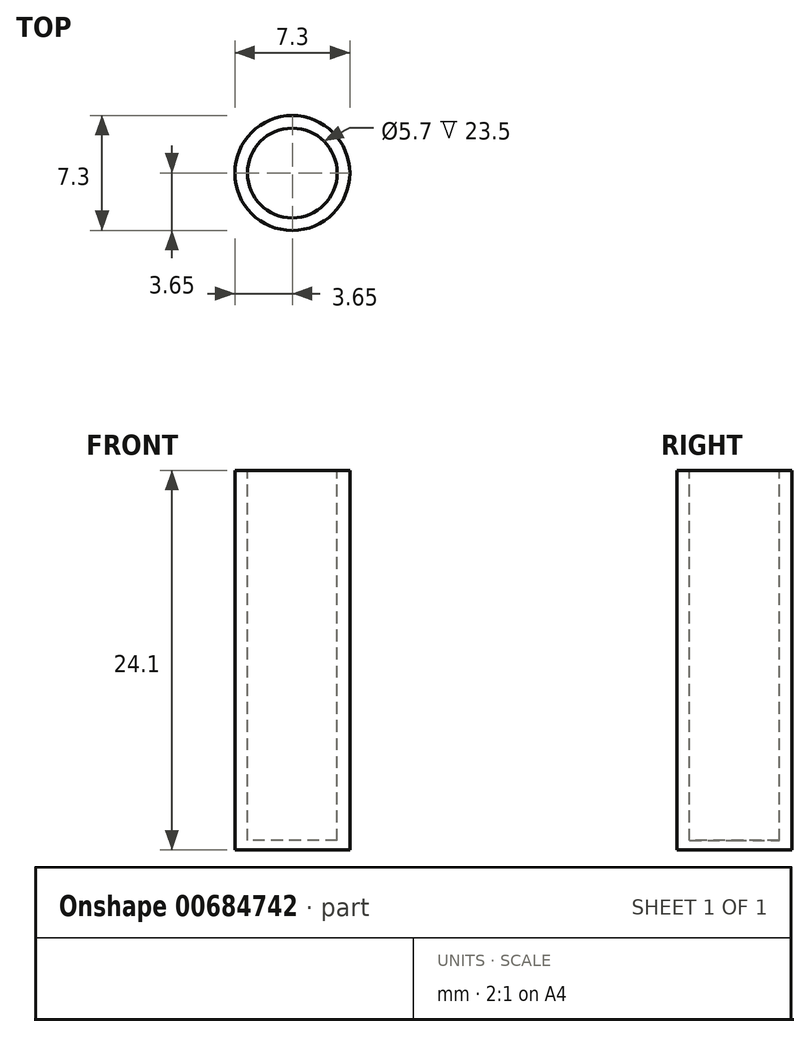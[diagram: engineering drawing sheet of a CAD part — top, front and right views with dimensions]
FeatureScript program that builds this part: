
annotation { "Feature Type Name" : "Feature", "Feature Type Description" : "" }
export const myFeature = defineFeature(function(context is Context, id is Id, definition is map)
    precondition{}
    {
        {
            var Q0;
            Q0=qCreatedBy(makeId("Front.planeOp"),FACE);
            var sketch = newSketch(context, id + "F0", { "sketchPlane" : qUnion([Q0])});
            skLineSegment(sketch, "E0", {"start": v(0, 0.6) * mm, "end": v(0, 0) * mm});
            skLineSegment(sketch, "E1", {"start": v(0, 0) * mm, "end": v(3.65, 0) * mm});
            skLineSegment(sketch, "E2", {"start": v(0, 0.6) * mm, "end": v(2.85, 0.6) * mm});
            skLineSegment(sketch, "E3", {"start": v(2.85, 0.6) * mm, "end": v(2.85, 24.1) * mm});
            skLineSegment(sketch, "E4", {"start": v(2.85, 24.1) * mm, "end": v(3.65, 24.1) * mm});
            skLineSegment(sketch, "E5", {"start": v(3.65, 24.1) * mm, "end": v(3.65, 0) * mm});
            skSolve(sketch);
        }
        {
            var Q0;
            Q0=qSketchRegion(id+"F0",true);
            var Q1;
            Q1=sQuery(id+"F0.wireOp",EDGE,"E0");
            revolve(context, id + "F1", {"entities" : qUnion([Q0]), "axis" : qUnion([Q1]), "revolveType" : RevolveType.FULL});
        }
    });
